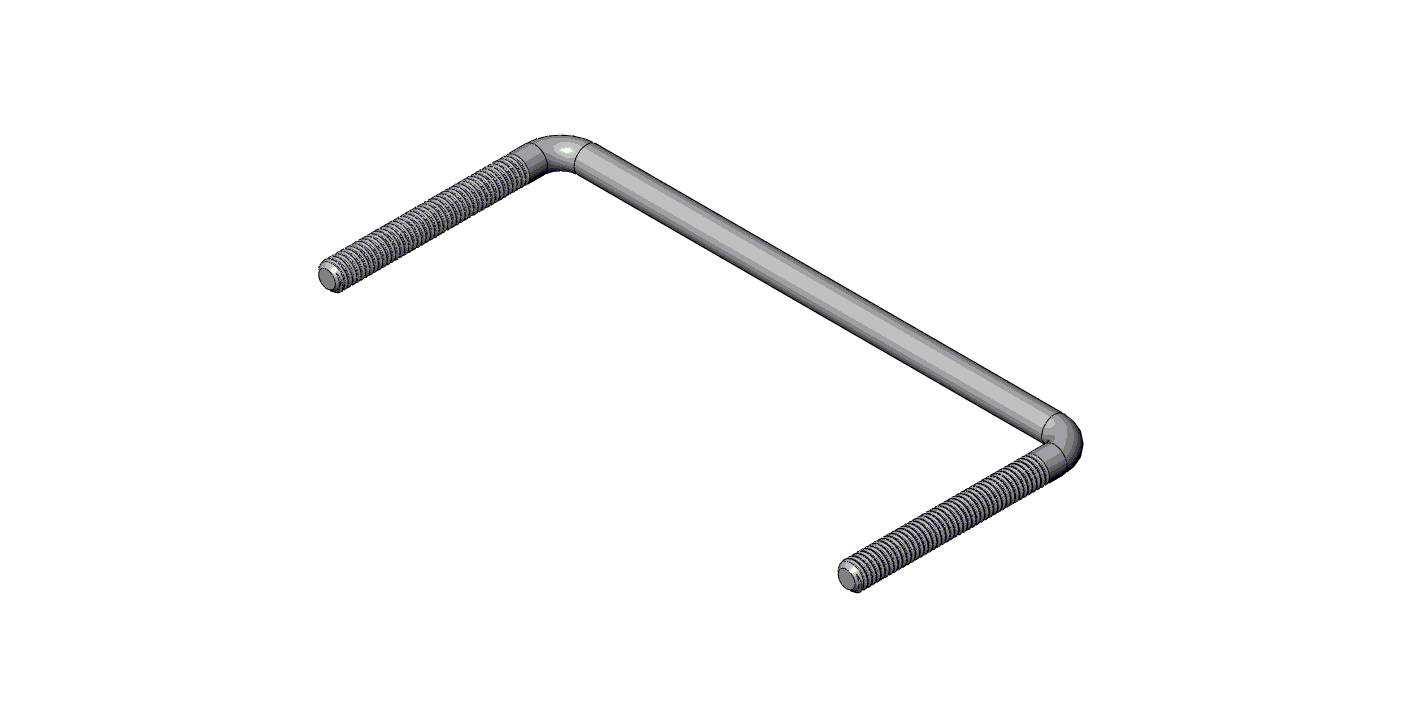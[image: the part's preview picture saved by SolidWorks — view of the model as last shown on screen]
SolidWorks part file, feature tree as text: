
SOLIDWORKS PART (.sldprt)
format: sldprt  version: not decoded by parser v0  size: 557,056 bytes
history: native  units: mm
features: sketch x6, sweep x3, helix x2, material x1, chamfer x1, plane x1 (+13 scaffold rows collapsed)
feature tree (27):
  scaffold x13  (default folders/planes/origin — collapsed)
  material  "Plain Carbon Steel"
  sketch  "Sketch1"  dims[D1=~5.91666mm]
  sketch  "Sketch3"  dims[D1=45.0mm D2=24.0mm]
  sweep  "Sweep1"
  chamfer  "Chamfer1"  Distance=0.5mm Angle=45deg
  plane  "Plane3"  Offset=22mm
  sketch  "Sketch11"
  helix  "Helix/Spiral3"  Pitch=30mm
  sketch  "Sketch12"  dims[c1.D1=~0.577581mm c2.D1=60.0deg c2.D2=0.8mm]
  sweep  "Cut-Sweep9"
  sketch  "Sketch13"
  helix  "Helix/Spiral4"  Pitch=30mm
  sketch  "Sketch14"  dims[c1.D1=0.0722mm c1.D2=~0.578779mm c2.D2=60.0deg c2.D3=0.8mm]
  sweep  "Cut-Sweep10"
decode coverage: 7 of 12 modeling features carry decoded parameters
note: ~ marks probable driven/reference dimensions
note: suppression state not decoded; provenance and decode notes live in map.json
